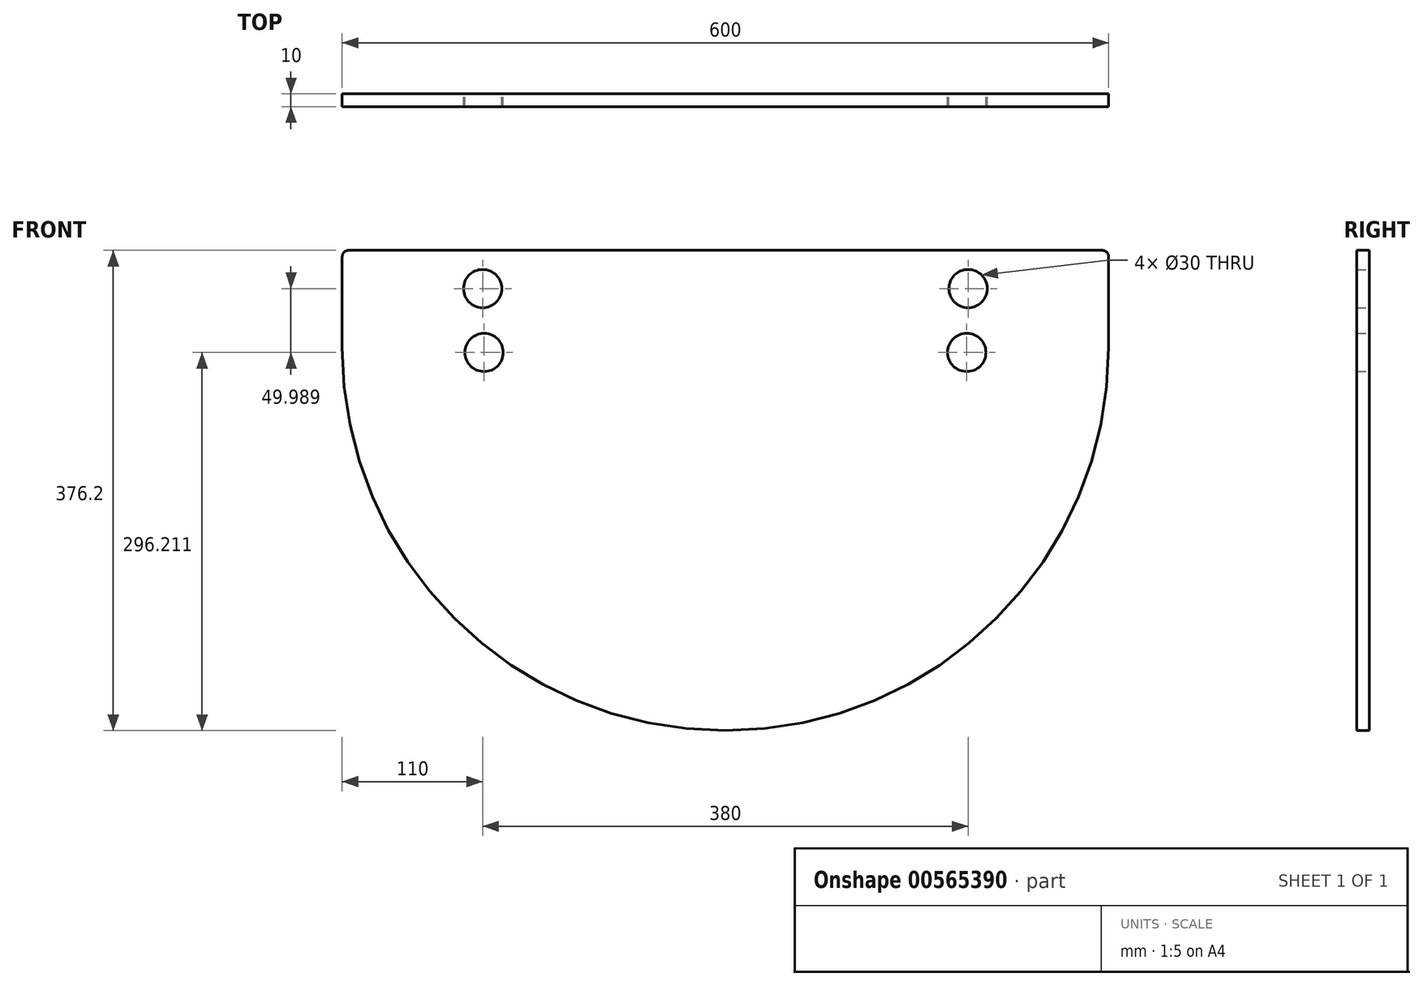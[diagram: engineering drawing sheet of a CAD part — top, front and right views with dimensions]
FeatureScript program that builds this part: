
annotation { "Feature Type Name" : "Feature", "Feature Type Description" : "" }
export const myFeature = defineFeature(function(context is Context, id is Id, definition is map)
    precondition{}
    {
        {
            var Q0;
            Q0=qCreatedBy(makeId("Front.planeOp"),FACE);
            var sketch = newSketch(context, id + "F0", { "sketchPlane" : qUnion([Q0])});
            skArc(sketch, "E0", {"start": v(-300, 0) * mm, "mid": v(0, -300) * mm, "end": v(300, 0) * mm});
            skLineSegment(sketch, "E1", {"start": v(-300, 0) * mm, "end": v(-300, 71.2) * mm});
            skLineSegment(sketch, "E2", {"start": v(-295, 76.2) * mm, "end": v(295, 76.2) * mm});
            skLineSegment(sketch, "E3", {"start": v(300, 0) * mm, "end": v(300, 71.2) * mm});
            skCircle(sketch, "E4", {"center": v(-190, 46.2) * mm, "radius": 15 * mm});
            skCircle(sketch, "E5", {"center": v(-188.96, -3.79) * mm, "radius": 15 * mm});
            skLineSegment(sketch, "E6", {"start": v(0, 0) * mm, "end": v(0, 58.87) * mm});
            skPoint(sketch, "E6.endSnap0", {"position": v(0, 76.2) * mm});
            skCircle(sketch, "E7.MirrorC", {"center": v(190, 46.2) * mm, "radius": 15 * mm});
            skCircle(sketch, "E8.MirrorC", {"center": v(188.96, -3.79) * mm, "radius": 15 * mm});
            skPoint(sketch, "E9.visualSharp", {"position": v(-300, 76.2) * mm});
            skArc(sketch, "E9.filletArc", {"start": v(-295, 76.2) * mm, "mid": v(-298.54, 74.74) * mm, "end": v(-300, 71.2) * mm});
            skPoint(sketch, "E10.visualSharp", {"position": v(300, 76.2) * mm});
            skArc(sketch, "E10.filletArc", {"start": v(300, 71.2) * mm, "mid": v(298.54, 74.74) * mm, "end": v(295, 76.2) * mm});
            skFitSpline(sketch, "E11", {"points": [v(-18.11, -299.45) * mm, v(-38.15, -254.57) * mm, v(-40.91, -222.78) * mm, v(-51.97, -212.41) * mm, v(-75.7, -208.85) * mm], "startDerivative": vector(-79.17, 134.68) * mm, "endDerivative": vector(-102.49, -8.18) * mm});
            skFitSpline(sketch, "E12.MirrorCS", {"points": [v(18.11, -299.45) * mm, v(38.15, -254.57) * mm, v(40.91, -222.78) * mm, v(51.97, -212.41) * mm, v(75.7, -208.85) * mm], "startDerivative": vector(79.17, 134.68) * mm, "endDerivative": vector(102.49, -8.18) * mm});
            skSolve(sketch);
        }
        {
            var Q0;
            {var subQ4=sQuery(id+"F0.wireOp",EDGE,"E1");Q0=makeQuery(id+"F0.imprint","IMPRINT",FACE,{"disambiguationData":[TD([[makeQuery(id+"F0.imprint","IMPRINT",EDGE,{"derivedFrom":subQ4}),-1.0]])]});}
            extrude(context, id + "F1", {"entities" : qUnion([Q0]), "depth" : 10 * mm, "offsetDistance" : 25 * mm});
        }
    });
